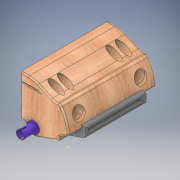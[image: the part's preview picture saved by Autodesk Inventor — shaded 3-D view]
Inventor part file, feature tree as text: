
AUTODESK INVENTOR PART (.ipt)
format: ipt  version: 2018 (Build 220112000, 112)  size: 786,944 bytes
history: native  units: in
note: dims shown in document units (in); Inventor stores cm internally (conversion verified against a paired STEP export)
features: sketch x25, extrude x23, projected_geometry x9, fillet x5
ambient origin geometry x8: Origin, YZ Plane, XZ Plane, XY Plane, X Axis, Y Axis, Z Axis, Center Point
bodies: Solid1 (feature_tree)
feature tree (62):
  extrude  "Extrusion1"  Depth=1.208in
  extrude  "Extrusion2"  Depth=0.41in
  extrude  "Extrusion3"  Depth=0.502in
  extrude  "Extrusion4"  Depth=0.9in
  extrude  "Extrusion5"  Depth=0.125in
  extrude  "Extrusion6"  Depth=0.025in
  fillet  "Fillet1"  Radius=3.23in
  extrude  "Extrusion7"  Depth=0.075in
  fillet  "Fillet2"  Radius=1.605in
  extrude  "Extrusion8"  Depth=0.05in
  extrude  "Extrusion9"  Depth=2.735in TaperAngle=0.0deg
  extrude  "Extrusion10"  Depth=1.496in TaperAngle=0.0deg
  extrude  "Extrusion11"  Depth=0.05in
  extrude  "Extrusion12"  Depth=0.1in
  extrude  "Extrusion13"  Depth=0.274in
  extrude  "Extrusion14"  Depth=0.274in
  extrude  "Extrusion15"  Depth=0.274in
  extrude  "Extrusion16"  Depth=0.274in
  extrude  "Extrusion17"  Depth=0.274in
  extrude  "Extrusion18"  Depth=0.03in TaperAngle=0.0deg
  extrude  "Extrusion19"  Depth=0.5in TaperAngle=0.0deg
  extrude  "Extrusion20"  Depth=0.778in
  extrude  "Extrusion21"  Depth=0.05in TaperAngle=0.0deg
  fillet  "Fillet3"  Radius=0.05in
  sketch  "Sketch22"  dims[d59=0.395in d60=0.52in d61=0.52in]
  sketch  "Sketch23"  dims[d62=0.395in d63=0.05in d64=0.495in d65=0.0in]
  extrude  "Extrusion22"  Depth=0.52in
  fillet  "Fillet4"  Radius=0.52in
  extrude  "Extrusion23"  Depth=0.05in
  fillet  "Fillet5"  Radius=0.495in
  sketch  "Sketch1"  dims[d0=0.193in d1=1.208in]
  sketch  "Sketch2"  dims[d2=0.307in d3=0.41in]
  sketch  "Sketch3"  dims[d4=1.517in d9=0.502in]
  projected_geometry  "Projected Loop1"
  sketch  "Sketch4"  dims[d10=0.125in d11=0.9in]
  sketch  "Sketch5"  dims[d12=0.5in d13=0.125in]
  sketch  "Sketch6"  dims[d14=0.025in d15=0.025in d16=3.23in d17=0.0in]
  sketch  "Sketch7"  dims[d19=0.075in d20=0.075in d21=1.605in]
  sketch  "Sketch8"  dims[d22=0.8in d23=0.05in]
  sketch  "Sketch9"  dims[d24=0.03in d25=2.735in d26=0.0in]
  projected_geometry  "Projected Loop2"
  sketch  "Sketch10"  dims[d27=3.735in d28=0.0in d29=1.496in d30=0.0in]
  sketch  "Sketch11"  dims[d31=0.1in d32=0.05in]
  sketch  "Sketch12"  dims[d33=0.05in d34=0.1in]
  sketch  "Sketch13"  dims[d35=0.13in d36=0.0in d37=0.274in]
  projected_geometry  "Projected Loop3"
  sketch  "Sketch14"  dims[d38=0.118in d39=0.274in]
  sketch  "Sketch15"  dims[d40=0.118in d41=0.274in]
  sketch  "Sketch16"  dims[d42=0.118in d43=0.274in]
  sketch  "Sketch17"  dims[d44=0.118in d45=0.274in]
  projected_geometry  "Projected Loop4"
  sketch  "Sketch18"  dims[d46=0.274in d47=0.03in d48=0.0in]
  sketch  "Sketch19"  dims[d49=0.125in d50=0.5in d51=0.0in]
  projected_geometry  "Projected Loop5"
  sketch  "Sketch20"  dims[d52=0.125in d53=0.778in]
  sketch  "Sketch21"  dims[d54=0.07in d55=0.05in d56=0.0in d57=0.05in d58=0.0in]
  sketch  "Sketch24"  dims[d66=0.14in]
  sketch  "Sketch25"  dims[d67=0.65in d68=0.325in d69=0.095in d70=0.095in d71=0.727in d72=0.3635in d73=0.3635in d74=0.4216in d75=0.14in d76=0.65in d77=0.325in d78=0.495in d79=0.0in d80=0.307in d81=0.41in d82=0.06in d83=0.0in d84=0.06in d85=0.0in d86=0.295in d87=0.385in d88=0.0in d89=0.385in d90=0.0in d91=0.31in d92=0.06in d93=0.0in d94=0.06in d95=0.0in d96=0.285in d97=0.445in d98=0.0in d99=0.445in d100=0.0in d101=0.022in d102=0.022in d103=0.214in d104=0.0in d105=0.214in d106=0.0in d107=0.05in d108=0.7653in d109=0.3825in d110=0.425in d111=0.425in d112=0.444in d113=0.444in d114=0.444in d115=0.444in d116=0.123in d117=0.123in d118=0.123in d119=0.123in d120=0.346in d121=0.246in d122=0.346in d123=0.246in d124=1.485in d125=0.0in d126=0.123in d127=0.422in d128=0.422in d129=0.222in d130=0.222in d131=0.375in d132=0.0in d133=0.222in]
  projected_geometry  "Projected Loop6"
  projected_geometry  "Projected Loop7"
  projected_geometry  "Projected Loop8"
  projected_geometry  "Projected Loop9"
